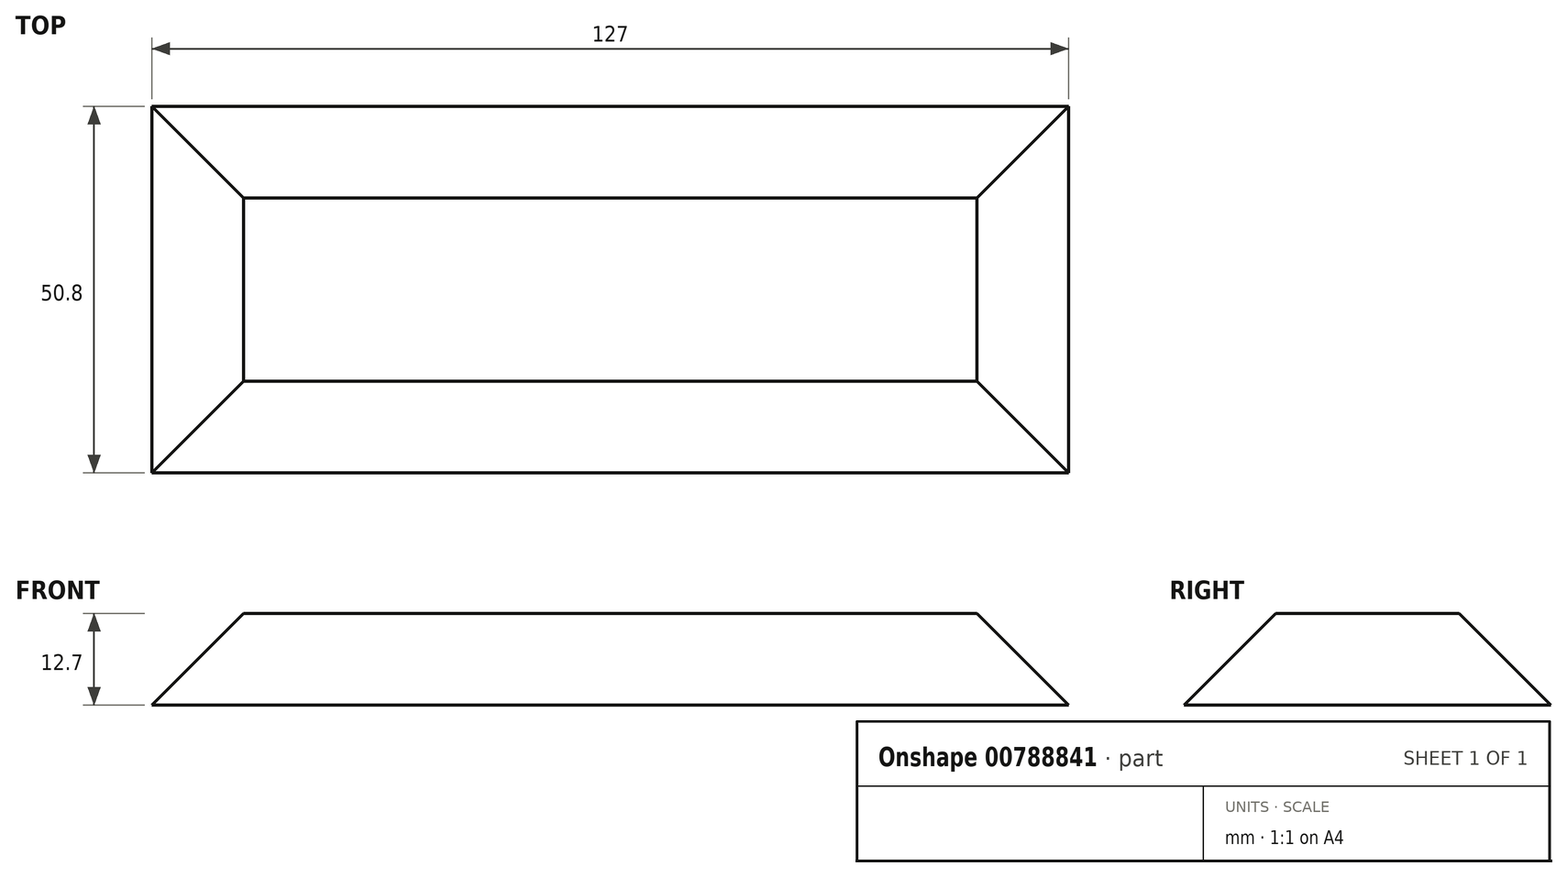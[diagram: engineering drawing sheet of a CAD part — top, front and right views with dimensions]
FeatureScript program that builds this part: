
annotation { "Feature Type Name" : "Feature", "Feature Type Description" : "" }
export const myFeature = defineFeature(function(context is Context, id is Id, definition is map)
    precondition{}
    {
        {
            var Q0;
            Q0=qCreatedBy(makeId("Front.planeOp"),FACE);
            var sketch = newSketch(context, id + "F0", { "sketchPlane" : qUnion([Q0])});
            skLineSegment(sketch, "E0.bottom", {"start": v(63.5, 12.7) * mm, "end": v(-63.5, 12.7) * mm});
            skLineSegment(sketch, "E0.right", {"start": v(-63.5, 12.7) * mm, "end": v(-63.5, 0) * mm});
            skPoint(sketch, "E0.middle", {"position": v(0, 0) * mm});
            skLineSegment(sketch, "E1", {"start": v(-63.5, 0) * mm, "end": v(63.5, 0) * mm});
            skLineSegment(sketch, "E2", {"start": v(63.5, 0) * mm, "end": v(63.5, 12.7) * mm});
            skSolve(sketch);
        }
        {
            var Q0;
            Q0 = qSketchRegion(id + "F0", true);
            extrude(context, id + "F1", {"entities" : qUnion([Q0]), "endBound" : BoundingType.SYMMETRIC, "depth" : 50.8 * mm, "offsetDistance" : 25.4 * mm});
        }
        {
            var Q0;
            Q0=makeQuery(id+"F1.opExtrude","SWEPT_FACE",FACE,{"disambiguationData":[OSD([sQuery(id+"F0.wireOp",EDGE,"E0.bottom")])]});
            chamfer(context, id + "F2", {"entities" : qUnion([Q0]), "chamferType" : ChamferType.OFFSET_ANGLE, "width" : 12.7 * mm, "oppositeDirection" : false, "angle" : 45 * degree, "tangentPropagation" : true});
        }
    });
